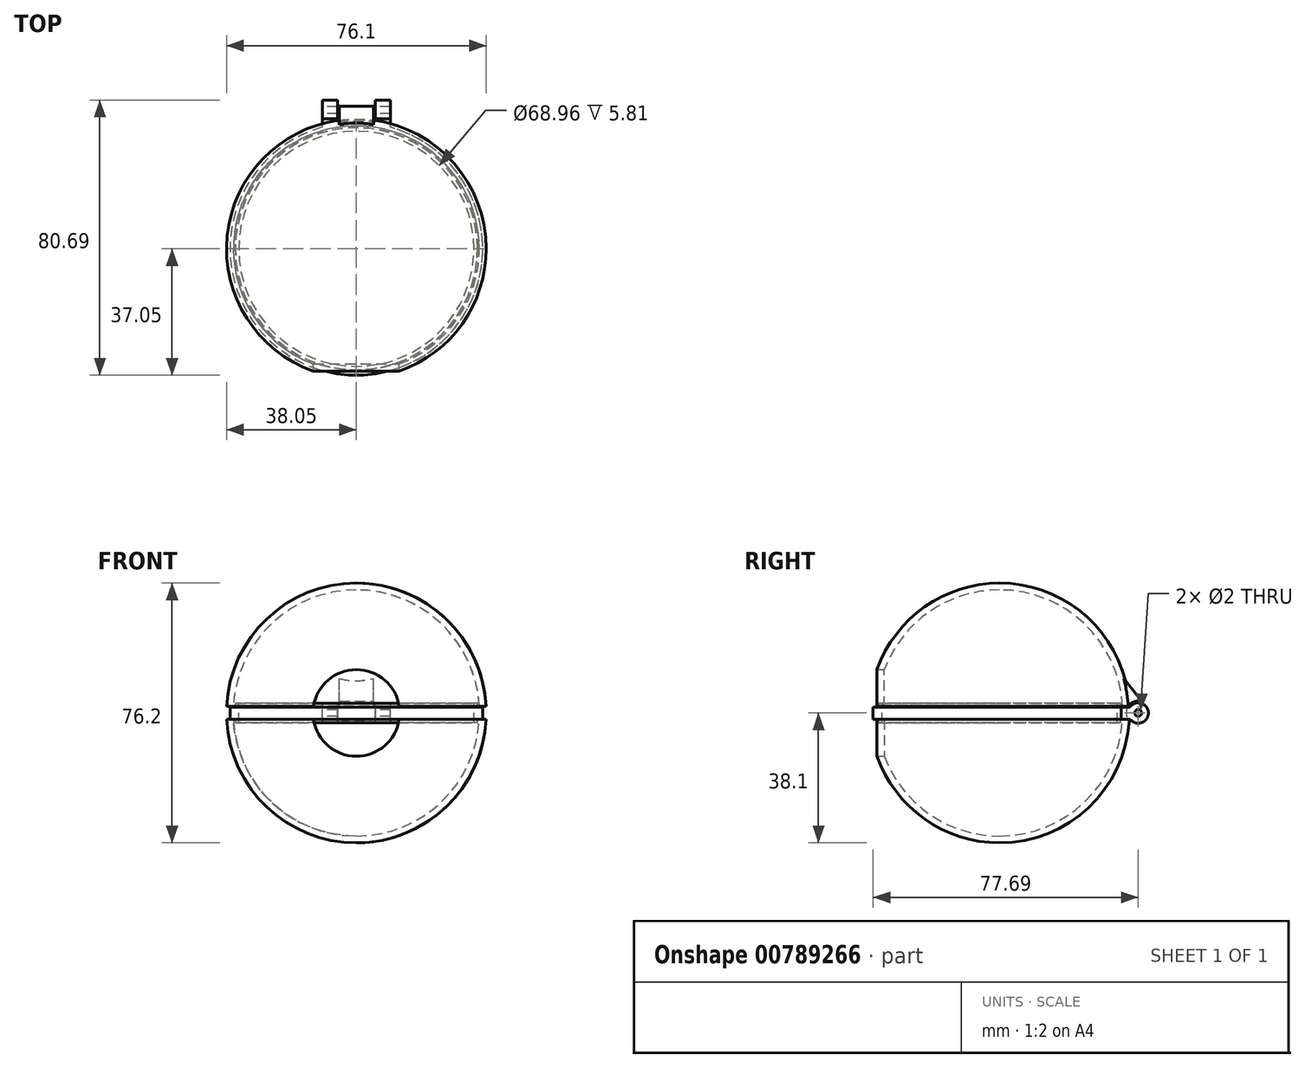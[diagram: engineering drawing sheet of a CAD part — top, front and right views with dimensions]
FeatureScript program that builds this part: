
annotation { "Feature Type Name" : "Feature", "Feature Type Description" : "" }
export const myFeature = defineFeature(function(context is Context, id is Id, definition is map)
    precondition{}
    {
        {
            var Q0;
            Q0=qCreatedBy(makeId("Front.planeOp"),FACE);
            var sketch = newSketch(context, id + "F0", { "sketchPlane" : qUnion([Q0])});
            skArc(sketch, "E0", {"start": v(0, -38.1) * mm, "mid": v(26.26, -27.6) * mm, "end": v(38.05, -1.9) * mm});
            skArc(sketch, "E1.0", {"start": v(0, -36.1) * mm, "mid": v(24.84, -26.2) * mm, "end": v(36.05, -1.9) * mm});
            skLineSegment(sketch, "E2", {"start": v(0, 38.1) * mm, "end": v(0, 36.1) * mm});
            skLineSegment(sketch, "E3.trimOffspring", {"start": v(0, -36.1) * mm, "end": v(0, -38.1) * mm});
            skLineSegment(sketch, "E4", {"start": v(0, 0) * mm, "end": v(33.36, 0) * mm, "construction": true});
            skArc(sketch, "E5.trimOffspring", {"start": v(36.05, 1.9) * mm, "mid": v(24.84, 26.2) * mm, "end": v(0, 36.1) * mm});
            skLineSegment(sketch, "E6.0", {"start": v(36.05, -1.9) * mm, "end": v(38.05, -1.9) * mm});
            skLineSegment(sketch, "E6.2", {"start": v(38.05, 1.9) * mm, "end": v(36.05, 1.9) * mm});
            skArc(sketch, "E7.trimOffspring", {"start": v(38.05, 1.9) * mm, "mid": v(26.26, 27.6) * mm, "end": v(0, 38.1) * mm});
            skSolve(sketch);
        }
        {
            var Q0;
            Q0 = qSketchRegion(id + "F0", true);
            var Q1;
            Q1=sQuery(id+"F0.wireOp",EDGE,"E2");
            revolve(context, id + "F1", {"surfaceOperationType" : NewSurfaceOperationType.NEW, "entities" : qUnion([Q0]), "axis" : qUnion([Q1]), "revolveType" : RevolveType.FULL});
        }
        {
            var Q0;
            Q0=qCreatedBy(makeId("Front.planeOp"),FACE);
            var sketch = newSketch(context, id + "F2", { "sketchPlane" : qUnion([Q0])});
            skCircle(sketch, "E8", {"center": v(0, 0) * mm, "radius": 12.7 * mm});
            skSolve(sketch);
        }
        {
            var Q0;
            Q0=qCreatedBy(makeId("Top.planeOp"),FACE);
            var sketch = newSketch(context, id + "F3", { "sketchPlane" : qUnion([Q0])});
            skLineSegment(sketch, "E9.bottom", {"start": v(-46.49, 40.96) * mm, "end": v(45.1, 40.96) * mm});
            skLineSegment(sketch, "E9.top", {"start": v(-46.49, -43.77) * mm, "end": v(45.1, -43.77) * mm});
            skLineSegment(sketch, "E9.left", {"start": v(-46.49, 40.96) * mm, "end": v(-46.49, -43.77) * mm});
            skLineSegment(sketch, "E9.right", {"start": v(45.1, 40.96) * mm, "end": v(45.1, -43.77) * mm});
            skSolve(sketch);
        }
        {
            var Q0;
            Q0 = qSketchRegion(id + "F3", true);
            extrude(context, id + "F4", {"entities" : qUnion([Q0]), "operationType" : NewBodyOperationType.REMOVE, "endBound" : BoundingType.SYMMETRIC, "oppositeDirection" : true, "depth" : .5 * mm, "offsetDistance" : 25.4 * mm});
        }
        {
            var Q0;
            Q0 = qSketchRegion(id + "F2", true);
            extrude(context, id + "F5", {"entities" : qUnion([Q0]), "operationType" : NewBodyOperationType.REMOVE, "depth" : 65.53 * mm, "offsetDistance" : 25.4 * mm});
        }
        {
            var Q0;
            Q0=qCreatedBy(makeId("Front.planeOp"),FACE);
            var sketch = newSketch(context, id + "F6", { "sketchPlane" : qUnion([Q0])});
            skLineSegment(sketch, "E10.0", {"start": v(37.05, 1.9) * mm, "end": v(38.05, 1.9) * mm, "construction": true});
            skLineSegment(sketch, "E11.0", {"start": v(37.05, -1.9) * mm, "end": v(38.05, -1.9) * mm, "construction": true});
            skLineSegment(sketch, "E12", {"start": v(37.05, 1.9) * mm, "end": v(37.05, -1.9) * mm});
            skPoint(sketch, "E13.orphan", {"position": v(-38.05, 1.9) * mm});
            skPoint(sketch, "E14.orphan", {"position": v(-38.05, -1.9) * mm});
            skLineSegment(sketch, "E15", {"start": v(37.05, 1.9) * mm, "end": v(35.55, 1.9) * mm, "construction": true});
            skArc(sketch, "E16", {"start": v(38.05, 1.9) * mm, "mid": v(37.63, 5.93) * mm, "end": v(36.8, 9.9) * mm, "construction": true});
            skArc(sketch, "E17.0", {"start": v(35.48, -2.9) * mm, "mid": v(35.52, -2.4) * mm, "end": v(35.55, -1.9) * mm});
            skLineSegment(sketch, "E18", {"start": v(37.05, -1.9) * mm, "end": v(35.55, -1.9) * mm});
            skArc(sketch, "E19.trimOffspring", {"start": v(35.56, 1.65) * mm, "mid": v(35.53, 2.28) * mm, "end": v(35.48, 2.9) * mm});
            skLineSegment(sketch, "E20", {"start": v(35.48, 2.9) * mm, "end": v(34.48, 2.9) * mm});
            skLineSegment(sketch, "E21", {"start": v(34.48, 2.9) * mm, "end": v(34.48, -2.9) * mm});
            skLineSegment(sketch, "E22", {"start": v(34.48, -2.9) * mm, "end": v(35.48, -2.9) * mm});
            skLineSegment(sketch, "E23", {"start": v(37.05, 0) * mm, "end": v(30.75, 0) * mm, "construction": true});
            skLineSegment(sketch, "E24", {"start": v(37.05, 1.65) * mm, "end": v(35.56, 1.65) * mm});
            skLineSegment(sketch, "E25", {"start": v(0, 0) * mm, "end": v(0, -18.62) * mm, "construction": true});
            skSolve(sketch);
        }
        {
            var Q0;
            Q0 = qSketchRegion(id + "F6", true);
            var Q1;
            Q1=sQuery(id+"F6.wireOp",EDGE,"E25");
            revolve(context, id + "F7", {"surfaceOperationType" : NewSurfaceOperationType.NEW, "entities" : qUnion([Q0]), "axis" : qUnion([Q1]), "revolveType" : RevolveType.FULL});
        }
        {
            var Q0;
            Q0=qCreatedBy(makeId("Right.planeOp"),FACE);
            var sketch = newSketch(context, id + "F8", { "sketchPlane" : qUnion([Q0])});
            skCircle(sketch, "E26", {"center": v(40.64, 0) * mm, "radius": 1 * mm});
            skArc(sketch, "E27", {"start": v(38.32, -1.9) * mm, "mid": v(43.64, 0.16) * mm, "end": v(38.14, 1.65) * mm});
            skLineSegment(sketch, "E28.0", {"start": v(35.1, 1.65) * mm, "end": v(38.14, 1.65) * mm});
            skLineSegment(sketch, "E28.1", {"start": v(35.1, -1.9) * mm, "end": v(38.32, -1.9) * mm});
            skLineSegment(sketch, "E29", {"start": v(35.1, 1.65) * mm, "end": v(35.1, -1.9) * mm});
            skPoint(sketch, "E30.orphan", {"position": v(-37.05, 1.65) * mm});
            skPoint(sketch, "E31.orphan", {"position": v(-35.92, -1.9) * mm});
            skSolve(sketch);
        }
        {
            var Q0;
            Q0 = qSketchRegion(id + "F8", true);
            extrude(context, id + "F9", {"entities" : qUnion([Q0]), "operationType" : NewBodyOperationType.ADD, "endBound" : BoundingType.SYMMETRIC, "depth" : 20 * mm, "offsetDistance" : 25.4 * mm});
        }
        {
            var Q0;
            Q0=qCreatedBy(makeId("Right.planeOp"),FACE);
            var sketch = newSketch(context, id + "F10", { "sketchPlane" : qUnion([Q0])});
            skCircle(sketch, "E32.0", {"center": v(40.64, 0) * mm, "radius": 1 * mm});
            skArc(sketch, "E33", {"start": v(38.07, 1.55) * mm, "mid": v(40.84, -3) * mm, "end": v(42.98, 1.87) * mm});
            skArc(sketch, "E34", {"start": v(38.07, 1.55) * mm, "mid": v(38.06, 1.73) * mm, "end": v(38.05, 1.9) * mm});
            skArc(sketch, "E35.0", {"start": v(36.55, 1.9) * mm, "mid": v(35.85, 7.39) * mm, "end": v(34.33, 12.7) * mm});
            skLineSegment(sketch, "E36", {"start": v(36.55, 1.9) * mm, "end": v(38.05, 1.9) * mm});
            skLineSegment(sketch, "E37", {"start": v(42.98, 1.87) * mm, "end": v(34.33, 12.7) * mm});
            skSolve(sketch);
        }
        {
            var Q0;
            Q0 = qSketchRegion(id + "F10", true);
            extrude(context, id + "F11", {"entities" : qUnion([Q0]), "operationType" : NewBodyOperationType.ADD, "endBound" : BoundingType.SYMMETRIC, "depth" : 10 * mm, "offsetDistance" : 25.4 * mm});
        }
        {
            var Q0;
            Q0=qCreatedBy(makeId("Right.planeOp"),FACE);
            var sketch = newSketch(context, id + "F12", { "sketchPlane" : qUnion([Q0])});
            skCircle(sketch, "E38.0", {"center": v(40.64, 0) * mm, "radius": 1 * mm});
            skCircle(sketch, "E39", {"center": v(40.64, 0) * mm, "radius": 3.5 * mm});
            skSolve(sketch);
        }
        {
            var Q0;
            Q0 = qSketchRegion(id + "F12", true);
            extrude(context, id + "F13", {"entities" : qUnion([Q0]), "operationType" : NewBodyOperationType.REMOVE, "endBound" : BoundingType.SYMMETRIC, "oppositeDirection" : true, "depth" : 11 * mm, "offsetDistance" : 25.4 * mm});
        }
    });
